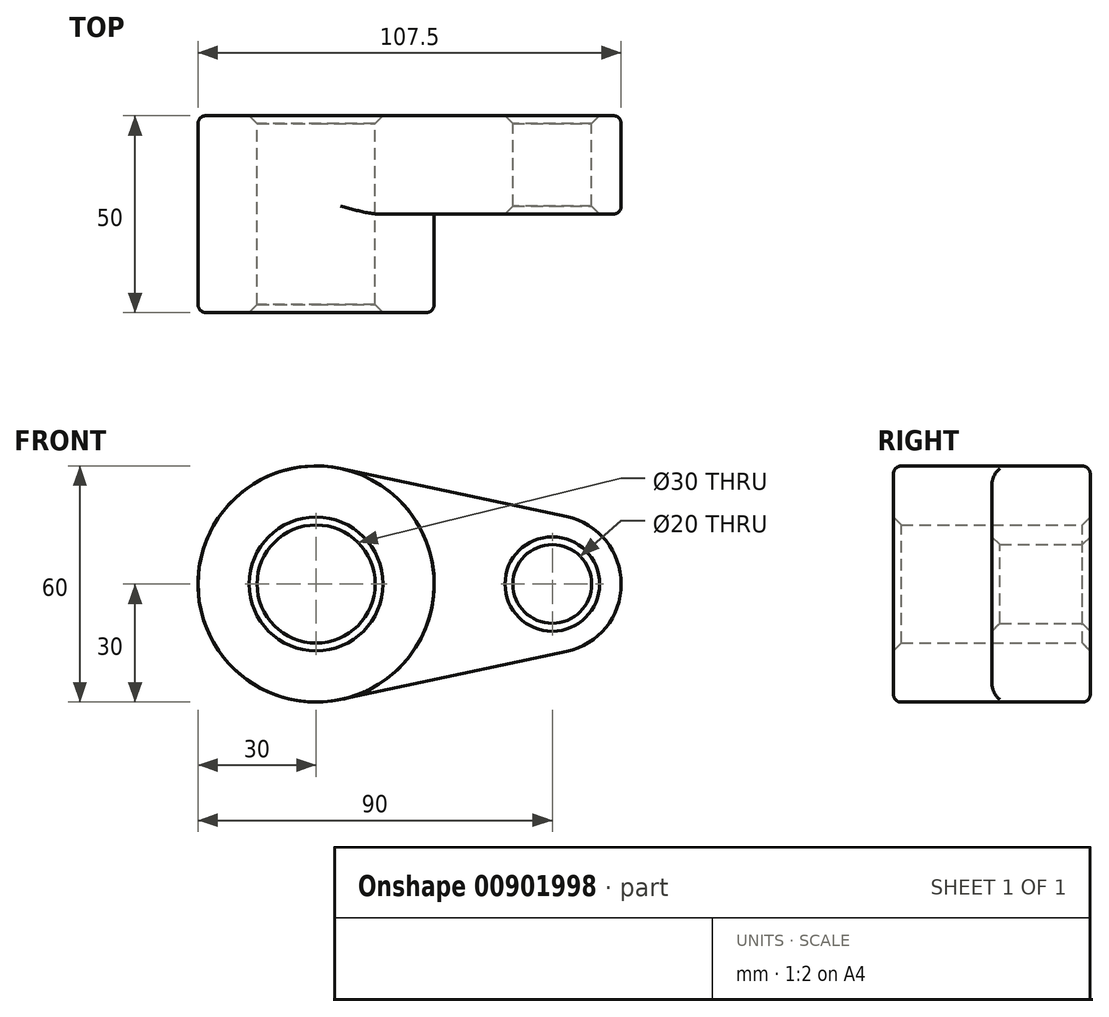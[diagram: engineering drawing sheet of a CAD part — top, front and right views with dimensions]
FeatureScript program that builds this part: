
annotation { "Feature Type Name" : "Feature", "Feature Type Description" : "" }
export const myFeature = defineFeature(function(context is Context, id is Id, definition is map)
    precondition{}
    {
        {
            var Q0;
            Q0=qCreatedBy(makeId("Front.planeOp"),FACE);
            var sketch = newSketch(context, id + "F0", { "sketchPlane" : qUnion([Q0])});
            skCircle(sketch, "E0", {"center": v(0, 0) * mm, "radius": 30 * mm});
            skCircle(sketch, "E1", {"center": v(60, 0) * mm, "radius": 17.5 * mm});
            skLineSegment(sketch, "E2", {"start": v(6.25, 29.34) * mm, "end": v(63.65, 17.12) * mm});
            skLineSegment(sketch, "E3", {"start": v(6.25, -29.34) * mm, "end": v(63.65, -17.12) * mm});
            skCircle(sketch, "E4", {"center": v(0, 0) * mm, "radius": 15 * mm});
            skCircle(sketch, "E5", {"center": v(60, 0) * mm, "radius": 10 * mm});
            skSolve(sketch);
        }
        {
            var Q0;
            Q0 = qSketchRegion(id + "F0", true);
            extrude(context, id + "F1", {"entities" : qUnion([Q0]), "depth" : 25 * mm, "offsetDistance" : 25 * mm});
        }
        {
            var Q0;
            Q0=makeQuery(id+"F0.imprint","IMPRINT",FACE,{"disambiguationData":[TD([[makeQuery(id+"F0.imprint","IMPRINT",EDGE,{"derivedFrom":sQuery(id+"F0.wireOp",EDGE,"E4")}),-1.0]])]});
            extrude(context, id + "F2", {"entities" : qUnion([Q0]), "operationType" : NewBodyOperationType.ADD, "depth" : 50 * mm, "offsetDistance" : 25 * mm});
        }
        {
            var Q0;
            Q0=makeQuery(id+"F1.opExtrude","CAP_EDGE",EDGE,{"disambiguationData":[OSD([sQuery(id+"F0.wireOp",EDGE,"E3")])],"isStart":true});
            var Q1;
            Q1=makeQuery(id+"F1.opExtrude","CAP_EDGE",EDGE,{"disambiguationData":[OSD([sQuery(id+"F0.wireOp",EDGE,"E3")])],"isStart":false});
            var Q2;
            Q2=makeQuery(id+"F2.opExtrude","CAP_EDGE",EDGE,{"disambiguationData":[OSD([sQuery(id+"F0.wireOp",EDGE,"E0")])],"isStart":false});
            fillet(context, id + "F3", {"entities" : qUnion([Q0, Q1, Q2]), "radius" : 2 * mm, "tangentPropagation" : true, "allowEdgeOverflow" : false});
        }
        {
            var Q0;
            Q0=makeQuery(id+"F2.opExtrude","CAP_EDGE",EDGE,{"disambiguationData":[OSD([sQuery(id+"F0.wireOp",EDGE,"E4")])],"isStart":false});
            var Q1;
            Q1=makeQuery(id+"F1.opExtrude","CAP_EDGE",EDGE,{"disambiguationData":[OSD([sQuery(id+"F0.wireOp",EDGE,"E5")])],"isStart":false});
            var Q2;
            Q2=makeQuery(id+"F1.opExtrude","CAP_EDGE",EDGE,{"disambiguationData":[OSD([sQuery(id+"F0.wireOp",EDGE,"E4")])],"isStart":true});
            var Q3;
            Q3=makeQuery(id+"F1.opExtrude","CAP_EDGE",EDGE,{"disambiguationData":[OSD([sQuery(id+"F0.wireOp",EDGE,"E5")])],"isStart":true});
            chamfer(context, id + "F4", {"entities" : qUnion([Q0, Q1, Q2, Q3]), "width" : 2 * mm, "tangentPropagation" : true});
        }
    });
